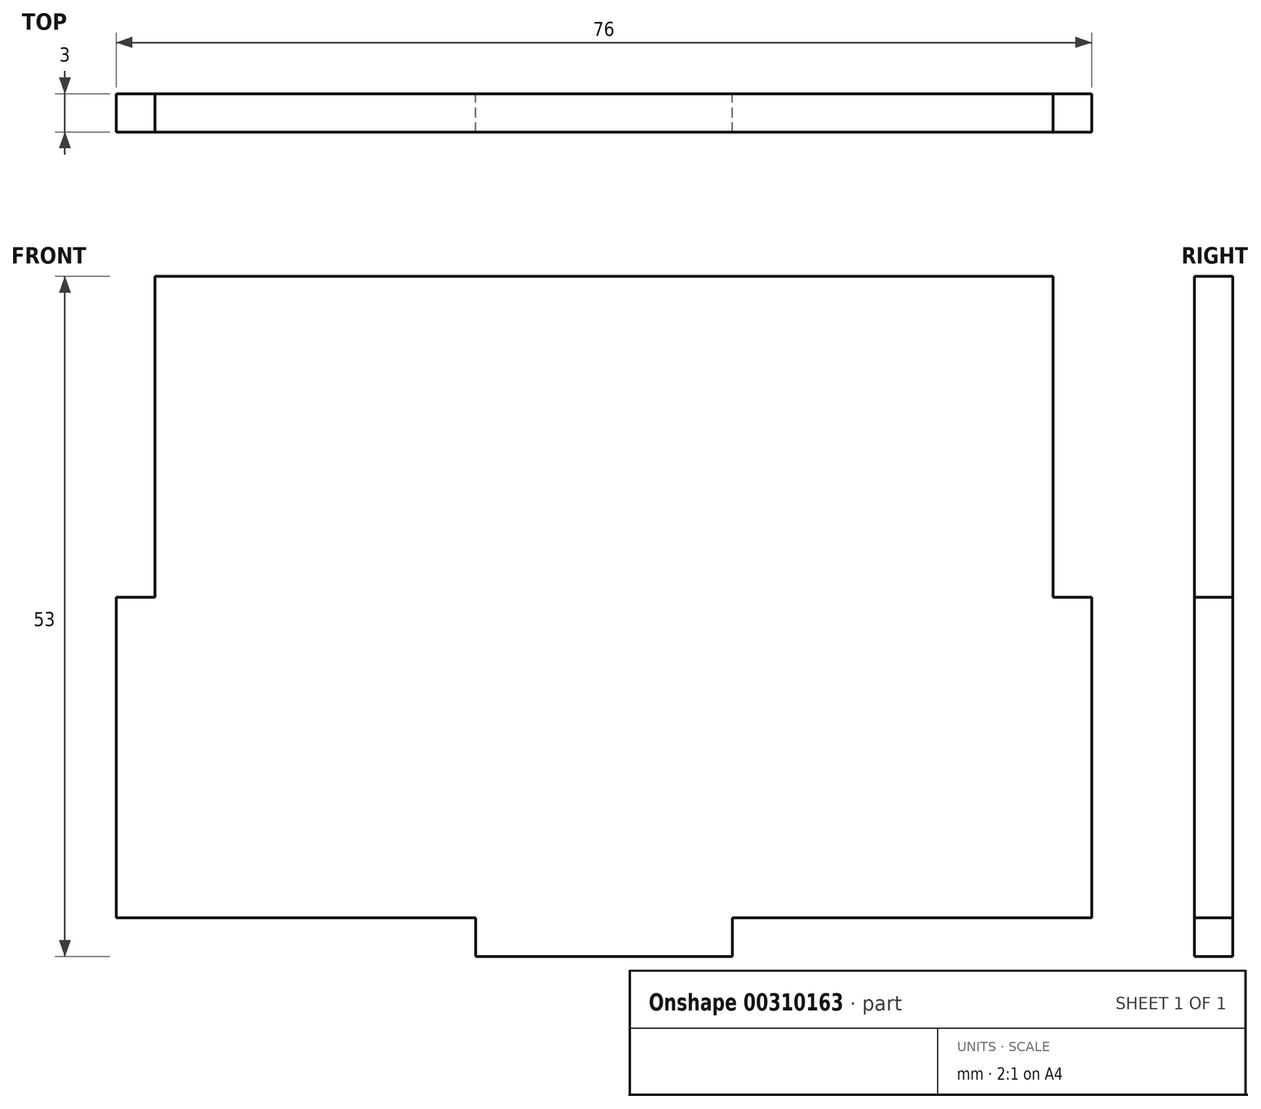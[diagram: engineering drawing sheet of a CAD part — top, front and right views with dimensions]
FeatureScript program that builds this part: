
annotation { "Feature Type Name" : "Feature", "Feature Type Description" : "" }
export const myFeature = defineFeature(function(context is Context, id is Id, definition is map)
    precondition{}
    {
        {
            var Q0;
            Q0=qCreatedBy(makeId("Front.planeOp"),FACE);
            var sketch = newSketch(context, id + "F0", { "sketchPlane" : qUnion([Q0])});
            skLineSegment(sketch, "E0.bottom", {"start": v(38, -25) * mm, "end": v(10, -25) * mm});
            skLineSegment(sketch, "E0.top", {"start": v(35, 25) * mm, "end": v(-35, 25) * mm});
            skLineSegment(sketch, "E0.left", {"start": v(38, -25) * mm, "end": v(38, 0) * mm});
            skLineSegment(sketch, "E0.right", {"start": v(-38, -25) * mm, "end": v(-38, 0) * mm});
            skPoint(sketch, "E0.middle", {"position": v(0, 0) * mm});
            skLineSegment(sketch, "E1.top", {"start": v(10, -28) * mm, "end": v(-10, -28) * mm});
            skLineSegment(sketch, "E1.left", {"start": v(10, -25) * mm, "end": v(10, -28) * mm});
            skLineSegment(sketch, "E1.right", {"start": v(-10, -25) * mm, "end": v(-10, -28) * mm});
            skLineSegment(sketch, "E2.trimOffspring", {"start": v(-10, -25) * mm, "end": v(-38, -25) * mm});
            skLineSegment(sketch, "E3.top", {"start": v(38, 0) * mm, "end": v(35, 0) * mm});
            skLineSegment(sketch, "E3.right", {"start": v(35, 25) * mm, "end": v(35, 0) * mm});
            skPoint(sketch, "E4.orphan", {"position": v(38, 25) * mm});
            skLineSegment(sketch, "E5.MirrorCS", {"start": v(-35, 25) * mm, "end": v(-35, 0) * mm});
            skLineSegment(sketch, "E6.MirrorCS", {"start": v(-38, 0) * mm, "end": v(-35, 0) * mm});
            skPoint(sketch, "E7.orphan", {"position": v(-38, 25) * mm});
            skSolve(sketch);
        }
        {
            var Q0;
            Q0 = qSketchRegion(id + "F0", true);
            extrude(context, id + "F1", {"entities" : qUnion([Q0]), "depth" : 3 * mm});
        }
    });
